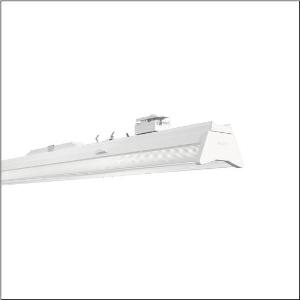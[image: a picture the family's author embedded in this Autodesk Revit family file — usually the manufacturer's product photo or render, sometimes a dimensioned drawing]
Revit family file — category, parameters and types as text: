
# Revit family: licross_r__21_performance_ho_52td16mn4e5m_6ed4
name_source: partatom
category: Lighting Fixtures
units: mm (PartAtom-declared; Revit-internal decimal feet)

## family parameters
Cut with Voids When Loaded = No
Host = Face
Light Source = No
Part Type = Normal
Room Calculation Point = No
Round Connector Dimension = Use Diameter
Shared = No

## types (1)
- --- (1 x LED, 14970 lm, 83.2 W, 4000K)
    Apparent Load = 83 VA
    CIE Flux Codes = 63 87 95 78 100
    Color Rendering = 80
    Color Temperature = 4000K
    Default Elevation = 1800 mm
    Description = Licross® 21 Performance HO, luminaire insert, of sheet steel, galvanised, coil coated, white, length: 1.500mm, width: 120mm, height: 123mm, LED rated luminous flux: 14.970lm, light colour: 840, SDCM (Standard Deviation of Colour Matching)MacAdam ≤ 3 SDCM (initial), control gear: ON/OFF Multilumen, with plug, 3-pole, with phase selection, mains connection: 220..240V, AC, 50/60Hz, rated input power: 83W, internal wiring halogen-free, primary light control with lens, of plastic, primary optical cover: cover, of PMMA, light emission: direct/indirect distribution, primary light characteristic: symmetric, protection rating (complete): IP54, insulation class (complete): insulation class I (protective earthing), certification: CE, ENEC, UKCA, protection symbol: D if used in an environment with non-conductive dust loads with corresponding accessories, impact resistance: IK06, permissible ambient temperature for indoor applications: -35..+35°C, corresponds to IFS (International Featured Standards) requirements for safety and quality in the food industry, reducing of maximum allowable ambient temperature of 5°C with ceiling mounting, LABS conformity tested according to VDMA 24364:2018-05, packaging unit: 1 piece
    Height = 114 mm
    Lamp = 1 x LED
    Lamp Light Flux = 14970 lm
    Lamp Power = 83.2 W
    Lamp count = 1
    Length = 1500 mm
    Luminous efficacy = 180 lm/W
    Manufacturer = Siteco
    ModVariant = No
    Model = 52TD16MN4E5M
    Mounting Place = Ceiling
    Mounting Type = Pendant
    Number of Poles = 1
    OnlyDefault = Yes
    Power Factor = 1
    Product Name = Licross® 21 Performance HO
    Product group = luminaire insert | ceiling pendant
    ProductGroupID = 901
    Protection Class = Protection class I
    Protection Degree = IP 54
    RLX_Detail_Level = 1
    RLX_Emergency_Light_Flux = 0 lm
    RLX_Emergency_Type = 0
    RLX_Emergency_Type_DB = No
    RlxData = <blob elided: 31945 chars, md5=7c3c9a03>
    Socket = socket
    Standby Power = 0 W
    System Light Flux = 14970 lm
    System Power = 83 W
    Type Comments = factory setting: luminous flux: 100 % | (A | C | E) | 195 mA
    Type Image = l_1256138.jpg
    URL = http://relux.com
    VarID = @adj_113143
    Voltage = 0 V
    Weight = 0.00 kg
    Width = 120 mm

## geometry (parser evidence)
native form markers: Blend x4, Sweep x11
no freeform markers — native parametric forms only
